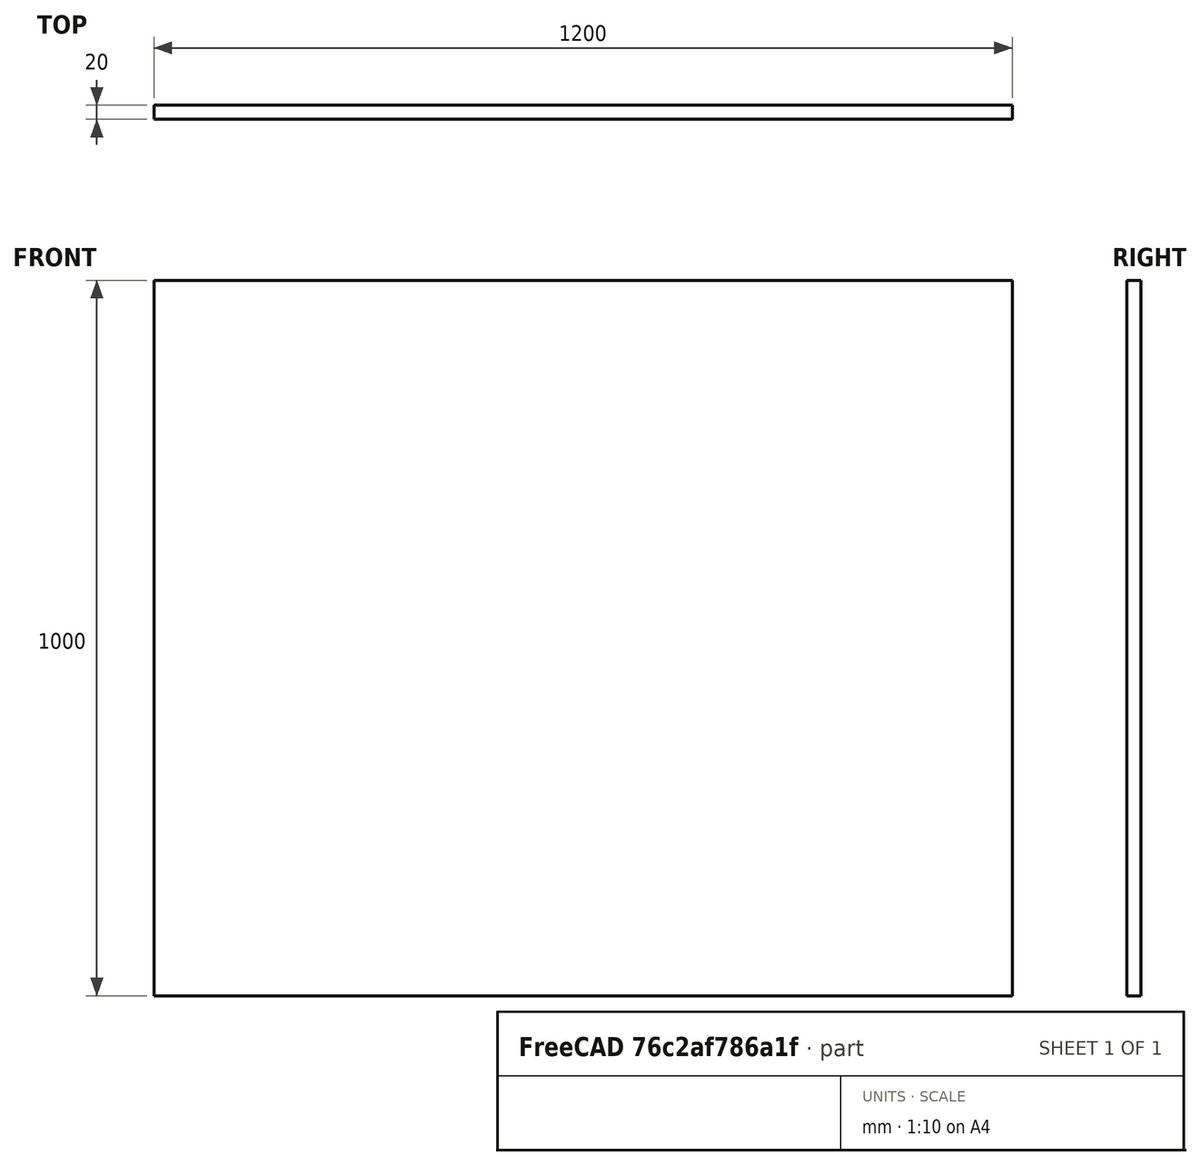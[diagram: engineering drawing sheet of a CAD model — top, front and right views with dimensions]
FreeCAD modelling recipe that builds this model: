
FCSTD DOCUMENT  (FreeCAD 0.19R)
Label: PAINEL
License: All rights reserved
LicenseURL: http://en.wikipedia.org/wiki/All_rights_reserved
objects: Sketcher::SketchObject×1, Part::Extrusion×1
note: 2 computed .brp shape members not serialized (recipe doc carries the construction recipe); baked Part::Feature solids carry a one-line shape summary decoded from their .brp

FEATURE [Sketcher::SketchObject] Sketch
  Placement = pos=(0,0,0) rot=(-1,0,0;4.71239rad)
  sketch-geometry (4):
    g0: LineSegment StartX=0 StartY=0 StartZ=0 EndX=1200 EndY=0 EndZ=0
    g1: LineSegment StartX=1200 StartY=0 StartZ=0 EndX=1200 EndY=1000 EndZ=0
    g2: LineSegment StartX=1200 StartY=1000 StartZ=0 EndX=0 EndY=1000 EndZ=0
    g3: LineSegment StartX=0 StartY=1000 StartZ=0 EndX=0 EndY=0 EndZ=0
  constraints (11):
    c: Coincident(g0,g1)
    c: Coincident(g1,g2)
    c: Coincident(g2,g3)
    c: Coincident(g3,g0)
    c: Horizontal(g0)
    c: Horizontal(g2)
    c: Vertical(g1)
    c: Vertical(g3)
    c: Coincident(g0,g-1)
    c: DistanceX(g2,g2) = 1200
    c: DistanceY(g3,g3) = 1000
FEATURE [Part::Extrusion] Extrude
  Base = -> Sketch
  Dir = (0,-1,3e-16)
  DirMode = 2
  FaceMakerClass = Part::FaceMakerBullseye
  LengthFwd = 20
  LengthRev = 0
  Solid = true
  Symmetric = false
